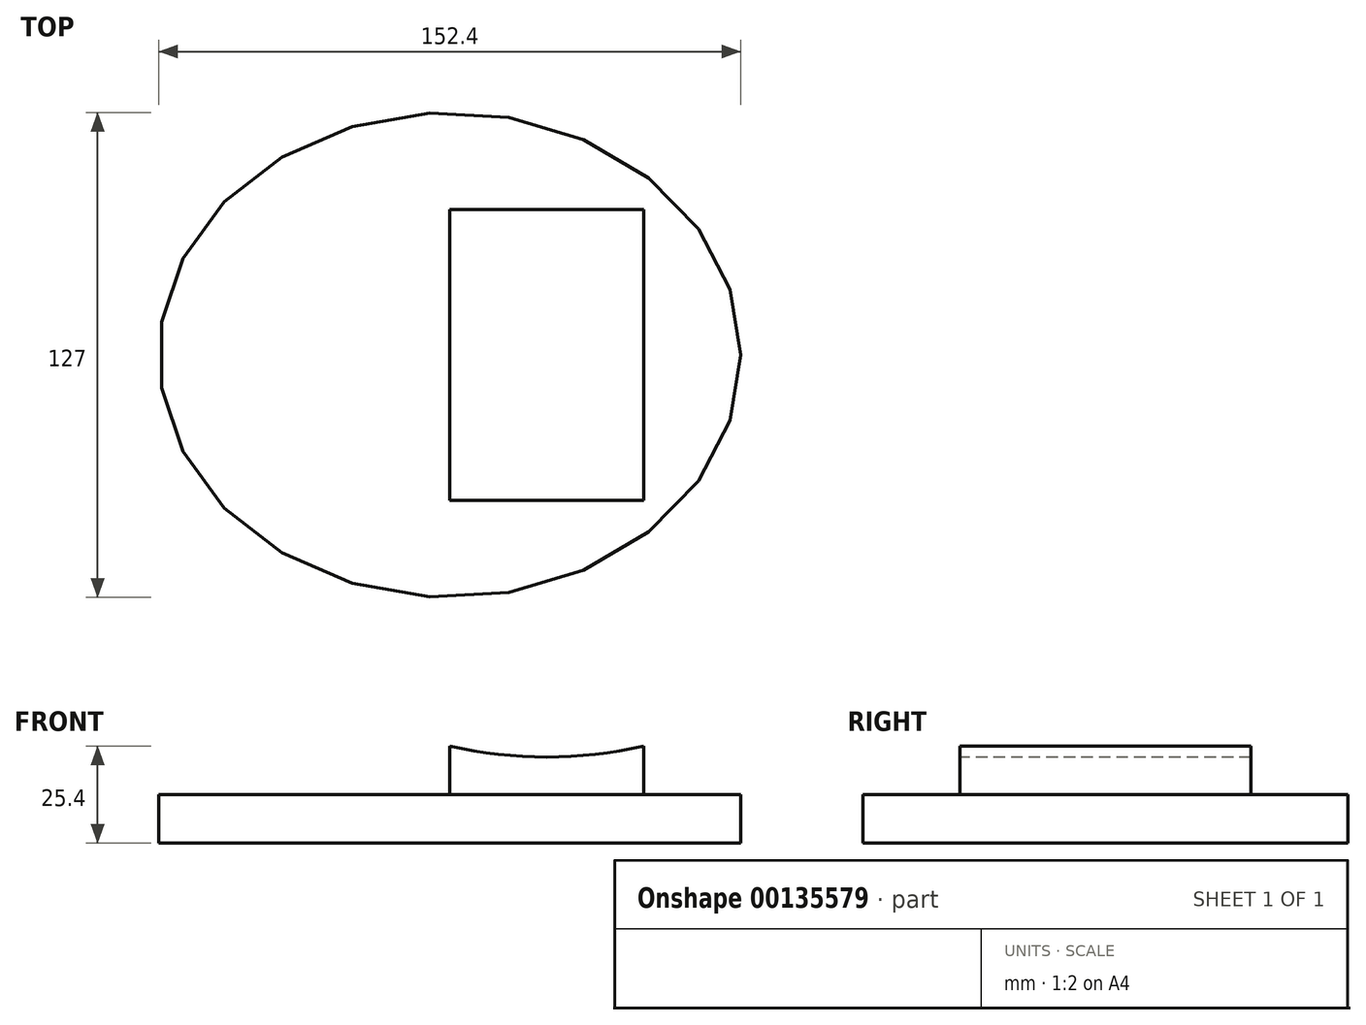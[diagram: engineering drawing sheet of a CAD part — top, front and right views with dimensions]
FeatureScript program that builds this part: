
annotation { "Feature Type Name" : "Feature", "Feature Type Description" : "" }
export const myFeature = defineFeature(function(context is Context, id is Id, definition is map)
    precondition{}
    {
        {
            var Q0;
            Q0=qCreatedBy(makeId("Top.planeOp"),FACE);
            var sketch = newSketch(context, id + "F0", { "sketchPlane" : qUnion([Q0])});
            skEllipse(sketch, "E0", {"center": v(0, 0) * mm, "majorRadius": 76.2 * mm, "minorRadius": 63.5 * mm, "majorAxis": v(1, 0)});
            skLineSegment(sketch, "E1", {"start": v(0, 0) * mm, "end": v(0, -38.1) * mm});
            skLineSegment(sketch, "E2", {"start": v(0, -38.1) * mm, "end": v(50.8, -38.1) * mm});
            skLineSegment(sketch, "E3", {"start": v(50.8, -38.1) * mm, "end": v(50.8, 38.1) * mm});
            skLineSegment(sketch, "E4", {"start": v(50.8, 38.1) * mm, "end": v(0, 38.1) * mm});
            skLineSegment(sketch, "E5", {"start": v(0, 38.1) * mm, "end": v(0, 0) * mm});
            skSolve(sketch);
        }
        {
            var Q0;
            Q0 = qSketchRegion(id + "F0", true);
            extrude(context, id + "F1", {"entities" : qUnion([Q0]), "depth" : 12.7 * mm});
        }
        {
            var Q0;
            Q0=makeQuery(id+"F0.imprint","IMPRINT",FACE,{"disambiguationData":[TD([[makeQuery(id+"F0.imprint","IMPRINT",EDGE,{"derivedFrom":sQuery(id+"F0.wireOp",EDGE,"E1")}),1.0]])]});
            extrude(context, id + "F2", {"entities" : qUnion([Q0]), "operationType" : NewBodyOperationType.ADD, "depth" : 25.4 * mm});
        }
        {
            var Q0;
            Q0=makeQuery(id+"F2.opExtrude","SWEPT_FACE",FACE,{"disambiguationData":[OSD([sQuery(id+"F0.wireOp",EDGE,"E2")])]});
            var sketch = newSketch(context, id + "F3", { "sketchPlane" : qUnion([Q0])});
            skArc(sketch, "E6", {"start": v(0, 25.4) * mm, "mid": v(25.4, 22.54) * mm, "end": v(50.8, 25.4) * mm});
            skSolve(sketch);
        }
        {
            var Q0;
            Q0 = qSketchRegion(id + "F3", true);
            var Q1;
            Q1=makeQuery(id+"F3.imprint","IMPRINT",FACE,{"disambiguationData":[TD([[makeQuery(id+"F3.imprint","IMPRINT",EDGE,{"derivedFrom":sQuery(id+"F3.wireOp",EDGE,"E6")}),1.0]])]});
            extrude(context, id + "F4", {"entities" : qUnion([Q0, Q1]), "operationType" : NewBodyOperationType.REMOVE, "endBound" : BoundingType.THROUGH_ALL, "oppositeDirection" : true, "depth" : 25.4 * mm});
        }
    });
